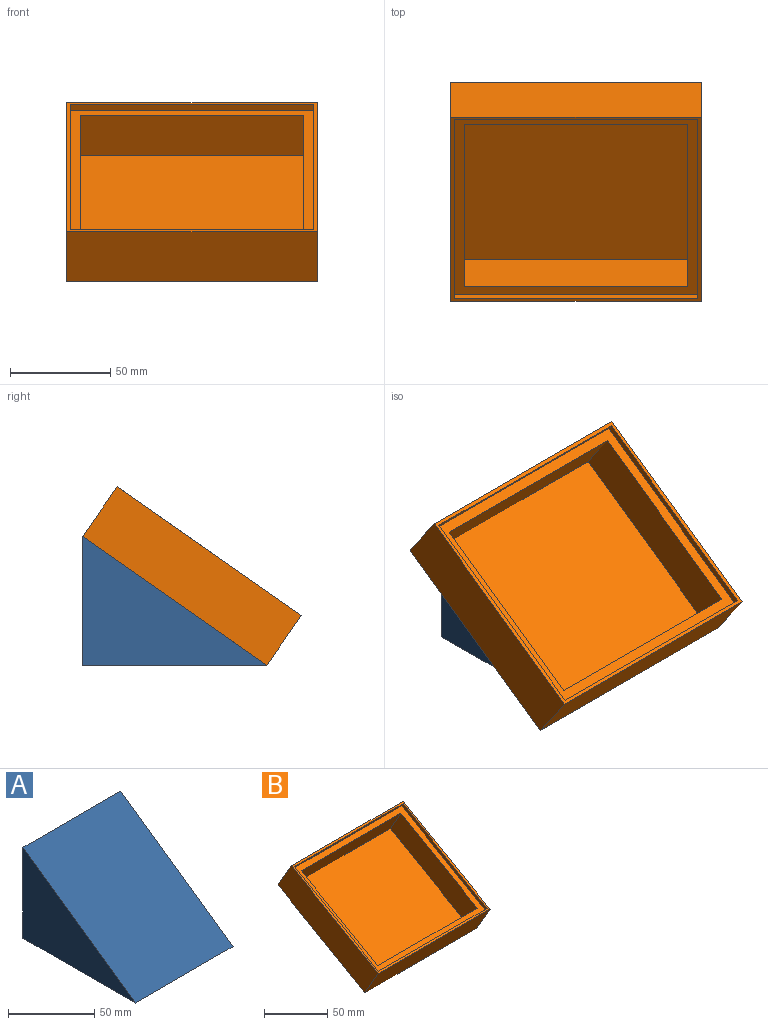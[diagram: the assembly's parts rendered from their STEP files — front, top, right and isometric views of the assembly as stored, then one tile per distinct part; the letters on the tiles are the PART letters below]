
ASSEMBLY  parts=2 mates=1
PART A: 24 faces, bbox 80x91.8x64.2 mm
  f0: plane 60x36mm, normal (0,0,-1), area 562.9mm2, adj f3,f8,f9,f10,f19,f20,f21,f22
  f1: plane 80x64.24mm, normal (0,1,0), area 5113.5mm2, adj f4,f5,f6,f7,f15,f16,f17,f18
  f2: plane 13x6.5mm, normal (0,-1,0), area 58.5mm2, adj f11,f12,f13,f14,f15,f16,f17,f18
  f3: plane 60x18mm, normal (0,-1,0), area 995.5mm2, adj f0,f4,f9,f10,f11,f12,f13,f14
  f4: plane 91.75x80mm, normal (0,0,-1), area 5180mm2, adj f1,f3,f5,f6,f7,f8,f9,f10
  f5: plane 91.75x80mm, normal (0,-0.57,0.82), area 8960.5mm2, adj f1,f4,f6,f7
  f6: plane 91.75x64.24mm, normal (1,0,0), area 2947.2mm2, adj f1,f4,f5
  f7: plane 91.75x64.24mm, normal (-1,0,0), area 2947.2mm2, adj f1,f4,f5
  f8: plane 60x18mm, normal (0,1,0), area 1080mm2, adj f0,f4,f9,f10
  f9: plane 36x18mm, normal (1,0,0), area 648mm2, adj f0,f3,f4,f8
  f10: plane 36x18mm, normal (-1,0,0), area 648mm2, adj f0,f3,f4,f8
  f11: plane 13x7mm, normal (0,0,-1), area 91mm2, adj f2,f3,f12,f14
  f12: plane 7x6.5mm, normal (1,0,0), area 45.5mm2, adj f2,f3,f11,f13
  f13: plane 13x7mm, normal (0,0,1), area 91mm2, adj f2,f3,f12,f14
  f14: plane 7x6.5mm, normal (-1,0,0), area 45.5mm2, adj f2,f3,f11,f13
  f15: plane 8x0.33mm, normal (0,0,-1), area 2.7mm2, adj f1,f2,f16,f18
  f16: plane 3.25x0.33mm, normal (-1,0,0), area 1.1mm2, adj f1,f2,f15,f17
  f17: plane 8x0.33mm, normal (0,0,1), area 2.7mm2, adj f1,f2,f16,f18
  f18: plane 3.25x0.33mm, normal (1,0,0), area 1.1mm2, adj f1,f2,f15,f17
  f19: plane 52.45x6mm, normal (0,1,0), area 314.7mm2, adj f0,f20,f22,f23
  f20: plane 30.45x6mm, normal (1,0,0), area 182.7mm2, adj f0,f19,f21,f23
  f21: plane 52.45x6mm, normal (0,-1,0), area 314.7mm2, adj f0,f20,f22,f23
  f22: plane 30.45x6mm, normal (-1,0,0), area 182.7mm2, adj f0,f19,f21,f23
  f23: plane 52.45x30.45mm, normal (0,0,-1), area 1597.1mm2, adj f19,f20,f21,f22
PART B: 16 faces, bbox 125x112x82 mm
  f0: plane 125x97mm, normal (0,-0.5,0.87), area 817.2mm2, adj f1,f2,f3,f4,f6,f7,f8,f9
  f1: plane 125x25.98mm, normal (0,-0.87,-0.5), area 3750mm2, adj f0,f2,f4,f5
  f2: plane 112x81.98mm, normal (1,0,0), area 3360mm2, adj f0,f1,f3,f5
  f3: plane 125x25.98mm, normal (0,0.87,0.5), area 3750mm2, adj f0,f2,f4,f5
  f4: plane 112x81.98mm, normal (-1,0,0), area 3360mm2, adj f0,f1,f3,f5
  f5: plane 125x97mm, normal (0,0.5,-0.87), area 14000mm2, adj f1,f2,f3,f4
  f6: plane 95.56x57.02mm, normal (1,0,0), area 347.2mm2, adj f0,f7,f9,f10
  f7: plane 121.5x2.77mm, normal (0,0.87,0.5), area 388.8mm2, adj f0,f6,f8,f10
  f8: plane 95.56x57.02mm, normal (-1,0,0), area 347.2mm2, adj f0,f7,f9,f10
  f9: plane 121.5x2.77mm, normal (0,-0.87,-0.5), area 388.8mm2, adj f0,f6,f8,f10
  f10: plane 121.5x93.96mm, normal (0,-0.5,0.87), area 2200mm2, adj f6,f7,f8,f9,f11,f12,f13,f14
  f11: plane 97.2x69.86mm, normal (1,0,0), area 2344.3mm2, adj f10,f12,f14,f15
  f12: plane 111.5x20.61mm, normal (0,0.87,0.5), area 2653.7mm2, adj f10,f11,f13,f15
  f13: plane 97.2x69.86mm, normal (-1,0,0), area 2344.3mm2, adj f10,f12,f14,f15
  f14: plane 111.5x20.61mm, normal (0,-0.87,-0.5), area 2653.7mm2, adj f10,f11,f13,f15
  f15: plane 111.5x85.3mm, normal (0,-0.5,0.87), area 10982.8mm2, adj f11,f12,f13,f14
PLACE A at identity fixed
PLACE B rot(axis=(1,0,0),5deg) t=(0,-5.31,4.88)mm
MATE fastened A.f5 <-> B.f5  axis (0,-0.57,0.82) through (0,30.64,64.24)mm
